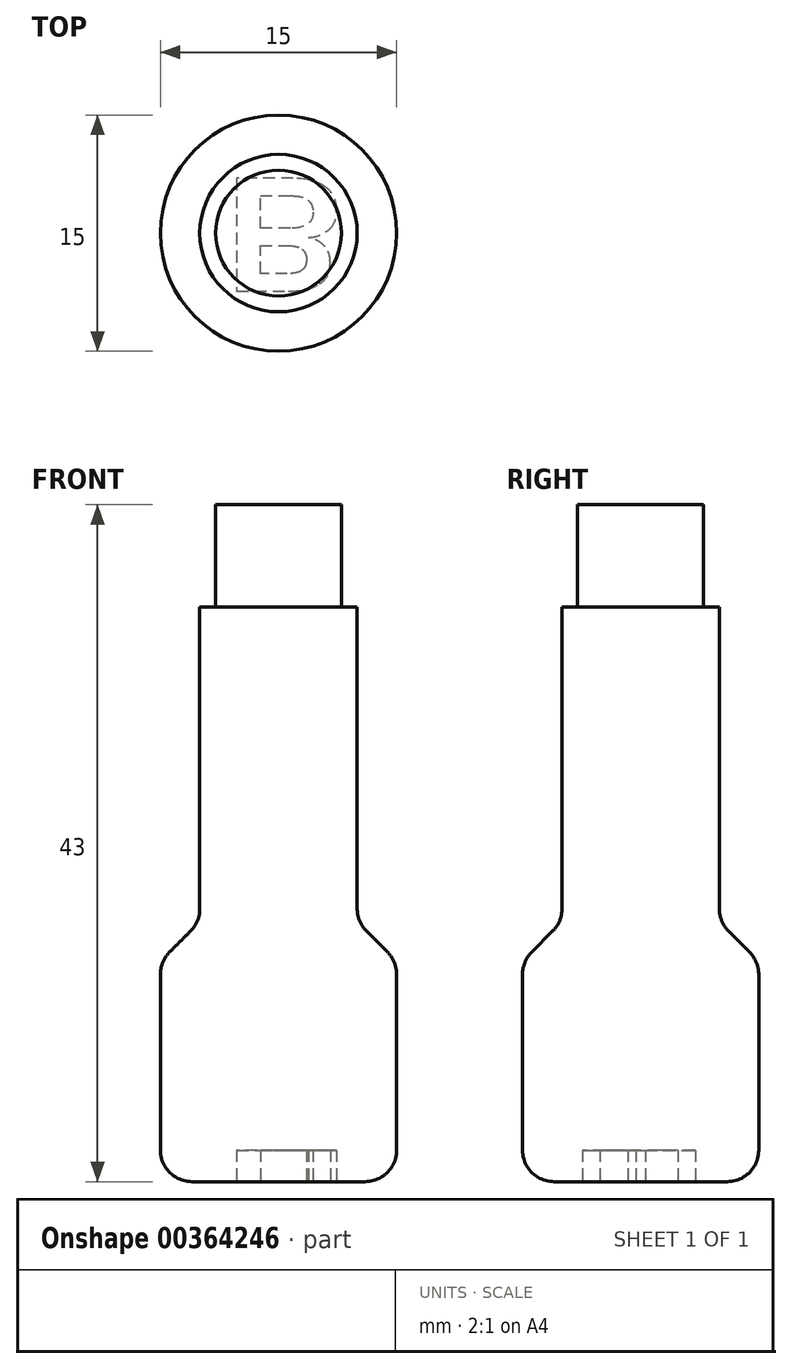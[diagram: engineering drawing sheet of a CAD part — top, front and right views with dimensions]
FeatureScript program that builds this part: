
annotation { "Feature Type Name" : "Feature", "Feature Type Description" : "" }
export const myFeature = defineFeature(function(context is Context, id is Id, definition is map)
    precondition{}
    {
        {
            var Q0;
            Q0=qCreatedBy(makeId("Right.planeOp"),FACE);
            var sketch = newSketch(context, id + "F0", { "sketchPlane" : qUnion([Q0])});
            skLineSegment(sketch, "E0", {"start": v(0, 0) * mm, "end": v(-7.5, 0) * mm});
            skLineSegment(sketch, "E1", {"start": v(-7.5, 0) * mm, "end": v(-7.5, 14) * mm});
            skLineSegment(sketch, "E2", {"start": v(-7.5, 14) * mm, "end": v(-5, 16.5) * mm});
            skLineSegment(sketch, "E3", {"start": v(-5, 16.5) * mm, "end": v(-5, 36.5) * mm});
            skLineSegment(sketch, "E4", {"start": v(-5, 36.5) * mm, "end": v(-4, 36.5) * mm});
            skLineSegment(sketch, "E5", {"start": v(-4, 36.5) * mm, "end": v(-4, 43) * mm});
            skLineSegment(sketch, "E6", {"start": v(-4, 43) * mm, "end": v(0, 43) * mm});
            skLineSegment(sketch, "E7", {"start": v(0, 43) * mm, "end": v(0, 0) * mm});
            skSolve(sketch);
        }
        {
            var Q0;
            Q0=makeQuery(id+"F0.imprint","IMPRINT",FACE,{"disambiguationData":[TD([[makeQuery(id+"F0.imprint","IMPRINT",EDGE,{"derivedFrom":sQuery(id+"F0.wireOp",EDGE,"E0")}),-1.0]])]});
            var Q1;
            Q1=sQuery(id+"F0.wireOp",EDGE,"E7");
            revolve(context, id + "F1", {"entities" : qUnion([Q0]), "axis" : qUnion([Q1]), "revolveType" : RevolveType.FULL});
        }
        {
            var Q0;
            Q0=makeQuery(id+"F1.opRevolve","SWEPT_EDGE",EDGE,{"disambiguationData":[OSD([sQuery(id+"F0.wireOp",EDGE,"E0"),sQuery(id+"F0.wireOp",EDGE,"E1")])]});
            var Q1;
            Q1=makeQuery(id+"F1.opRevolve","SWEPT_EDGE",EDGE,{"disambiguationData":[OSD([sQuery(id+"F0.wireOp",EDGE,"E1"),sQuery(id+"F0.wireOp",EDGE,"E2")])]});
            var Q2;
            Q2=makeQuery(id+"F1.opRevolve","SWEPT_EDGE",EDGE,{"disambiguationData":[OSD([sQuery(id+"F0.wireOp",EDGE,"E2"),sQuery(id+"F0.wireOp",EDGE,"E3")])]});
            fillet(context, id + "F2", {"entities" : qUnion([Q0, Q1, Q2]), "radius" : 2 * mm, "tangentPropagation" : true, "allowEdgeOverflow" : false});
        }
        {
            var Q0;
            Q0=makeQuery(id+"F1.opRevolve","SWEPT_FACE",FACE,{"disambiguationData":[OSD([sQuery(id+"F0.wireOp",EDGE,"E0")])]});
            var sketch = newSketch(context, id + "F3", { "sketchPlane" : qUnion([Q0])});
            skText(sketch, "E8", { "text": "B", "fontName": "Arimo-Bold.ttf"});
            const initialGuessF3  = {"E8": [-0.00335, -0.00348, 1, 0, 0.0075]};
            skSetInitialGuess(sketch, initialGuessF3);
            skSolve(sketch);
        }
        {
            var Q0;
            Q0 = qSketchRegion(id + "F3", true);
            extrude(context, id + "F4", {"entities" : qUnion([Q0]), "operationType" : NewBodyOperationType.REMOVE, "oppositeDirection" : true, "depth" : 2 * mm});
        }
    });
